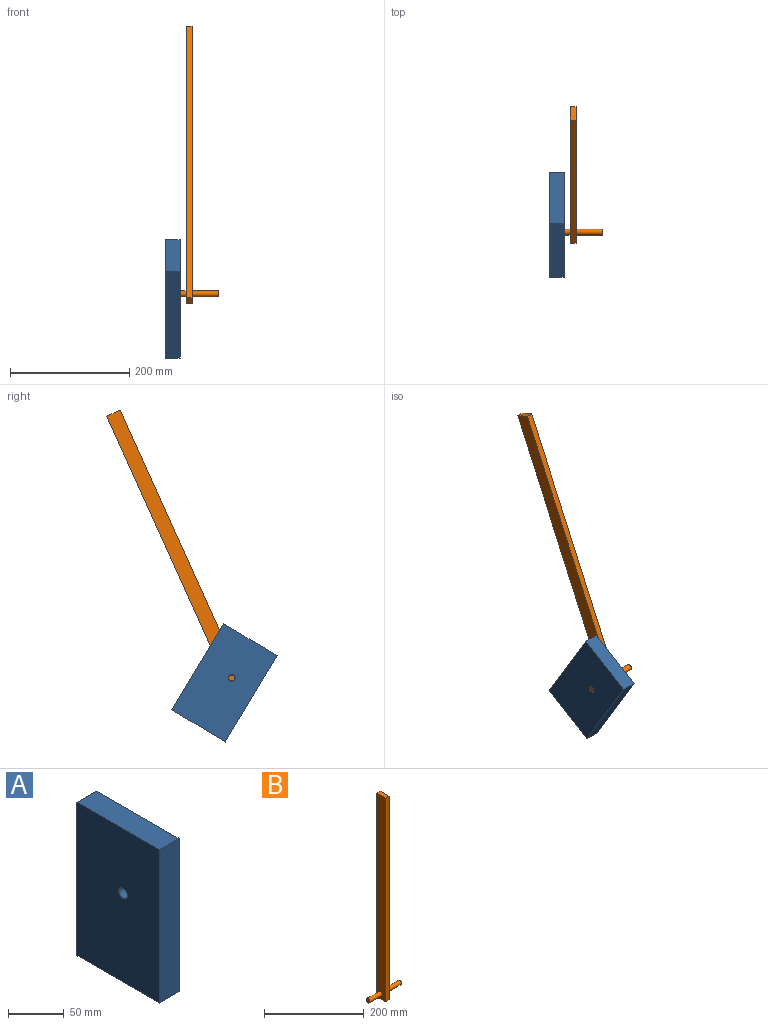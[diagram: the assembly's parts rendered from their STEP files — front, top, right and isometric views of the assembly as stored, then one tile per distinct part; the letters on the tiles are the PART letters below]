
ASSEMBLY  parts=2 mates=1
PART A: 7 faces, bbox 25x104.9x168.8 mm
  f0: plane 104.86x25mm, normal (0,0,1), area 2621.5mm2, adj f1,f3,f4,f5
  f1: plane 168.79x25mm, normal (0,-1,0), area 4219.7mm2, adj f0,f2,f4,f5
  f2: plane 104.86x25mm, normal (0,0,-1), area 2621.5mm2, adj f1,f3,f4,f5
  f3: plane 168.79x25mm, normal (0,1,0), area 4219.7mm2, adj f0,f2,f4,f5
  f4: plane 168.79x104.86mm, normal (1,0,0), area 17604.1mm2, adj f0,f1,f2,f3,f6
  f5: plane 168.79x104.86mm, normal (-1,0,0), area 17604.1mm2, adj f0,f1,f2,f3,f6
  f6: cylinder r=5.5mm len=25mm, axis (1,0,0), area 863.9mm2, adj f4,f5
PART B: 10 faces, bbox 90x25x500 mm
  f0: plane 500x10mm, normal (0,-1,0), area 5000mm2, adj f1,f3,f4,f5
  f1: plane 25x10mm, normal (0,0,-1), area 250mm2, adj f0,f2,f4,f5
  f2: plane 500x10mm, normal (0,1,0), area 5000mm2, adj f1,f3,f4,f5
  f3: plane 25x10mm, normal (0,0,1), area 250mm2, adj f0,f2,f4,f5
  f4: plane 500x25mm, normal (1,0,0), area 12421.5mm2, adj f0,f1,f2,f3,f8
  f5: plane 500x25mm, normal (-1,0,0), area 12421.5mm2, adj f0,f1,f2,f3,f7
  f6: plane 10x10mm, normal (-1,0,0), area 78.5mm2, adj f7
  f7: cylinder r=5mm len=35mm, axis (-1,0,0), area 1099.6mm2, adj f5,f6
  f8: cylinder r=5mm len=45mm, axis (-1,0,0), area 1413.7mm2, adj f4,f9
  f9: plane 10x10mm, normal (1,0,0), area 78.5mm2, adj f8
PLACE A rot(axis=(1,0,0),31.1deg) t=(19.55,-79.93,33.29)mm
PLACE B rot(axis=(-1,0,0),24.3deg) t=(33.47,-81.06,-28.16)mm
MATE cylindrical B.f7 <-> A.f6  axis (-1,0,0) through (19.55,-71.5,19.32)mm
